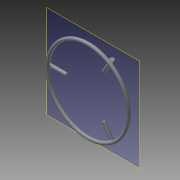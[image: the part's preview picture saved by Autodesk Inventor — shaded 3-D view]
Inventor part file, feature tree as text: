
AUTODESK INVENTOR PART (.ipt)
format: ipt  version: 2014 (Build 180170000, 170)  size: 156,672 bytes
history: native  units: mm
features: sketch x4, extrude x3, plane x2, revolve x1, other x1, pattern_circular x1
ambient origin geometry x8: Origin, YZ Plane, XZ Plane, XY Plane, X Axis, Y Axis, Z Axis, Center Point
bodies: Solid1 (feature_tree)
feature tree (12):
  revolve  "Revolution1"  [1 undecoded]
  plane  "Work Plane1"
  extrude  "Extrusion1"  TaperAngle=90.0deg  [1 undecoded]
  extrude  "Extrusion2"  Depth=6.0mm
  other  "Work Axis1"
  pattern_circular  "Circular Pattern1"  [2 undecoded]
  plane  "Work Plane2"
  extrude  "Extrusion3"  Depth=6.0mm
  sketch  "Sketch1"  dims[d0=6.0mm d1=148.0mm]
  sketch  "Sketch2"  dims[d2=10.0mm d3=90.0deg]
  sketch  "Sketch3"  dims[d4=-3.0mm d5=6.0mm]
  sketch  "Sketch4"  dims[d6=6.0mm d7=6.0mm d8=6.0mm d9=6.0mm d10=0.0mm d11=6.0mm d12=26.0mm d13=0.0mm d14=30.0mm d15=360.0deg d17=9.0mm d18=91.0mm d19=74.0mm d20=26.0mm d21=0.0mm]
note: 4 required parameter values undecoded (feature->parameter linkage not recoverable at this tier; creation-order binding heuristic only, values carry confidence <= 0.55)